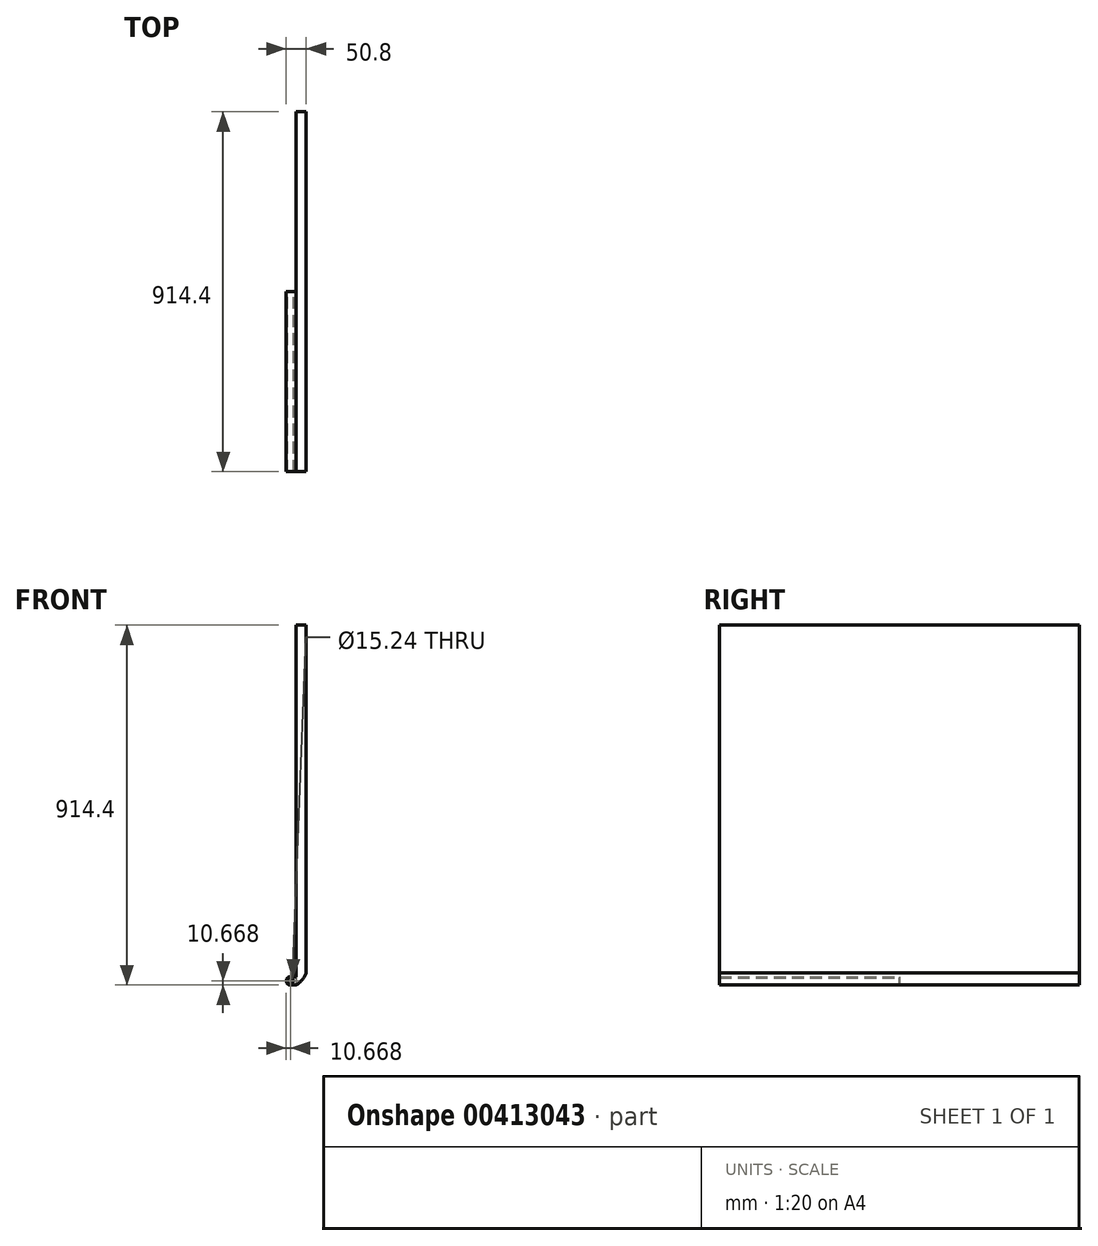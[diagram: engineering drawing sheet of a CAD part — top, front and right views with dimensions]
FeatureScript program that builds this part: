
annotation { "Feature Type Name" : "Feature", "Feature Type Description" : "" }
export const myFeature = defineFeature(function(context is Context, id is Id, definition is map)
    precondition{}
    {
        {
            var Q0;
            Q0=qCreatedBy(makeId("Right.planeOp"),FACE);
            var sketch = newSketch(context, id + "F0", { "sketchPlane" : qUnion([Q0])});
            skLineSegment(sketch, "E0.bottom", {"start": v(457.2, -457.2) * mm, "end": v(-457.2, -457.2) * mm});
            skLineSegment(sketch, "E0.top", {"start": v(457.2, 457.2) * mm, "end": v(-457.2, 457.2) * mm});
            skLineSegment(sketch, "E0.left", {"start": v(457.2, -457.2) * mm, "end": v(457.2, 457.2) * mm});
            skLineSegment(sketch, "E0.right", {"start": v(-457.2, -457.2) * mm, "end": v(-457.2, 457.2) * mm});
            skPoint(sketch, "E0.middle", {"position": v(0, 0) * mm});
            skSolve(sketch);
        }
        {
            var Q0;
            Q0=makeQuery(id+"F0.imprint","IMPRINT",FACE,{"disambiguationData":[TD([[makeQuery(id+"F0.imprint","IMPRINT",EDGE,{"derivedFrom":sQuery(id+"F0.wireOp",EDGE,"E0.bottom")}),-1.0]])]});
            extrude(context, id + "F1", {"entities" : qUnion([Q0]), "depth" : 25.4 * mm});
        }
        {
            var Q0;
            Q0=qCreatedBy(makeId("Front.planeOp"),FACE);
            var sketch = newSketch(context, id + "F2", { "sketchPlane" : qUnion([Q0])});
            skArc(sketch, "E1", {"start": v(-14.73, -435.86) * mm, "mid": v(-25.4, -446.53) * mm, "end": v(-14.73, -457.2) * mm});
            skLineSegment(sketch, "E2", {"start": v(-25.4, -446.53) * mm, "end": v(-25.4, -527.35) * mm, "construction": true});
            skLineSegment(sketch, "E3", {"start": v(0, -457.2) * mm, "end": v(-47.92, -457.2) * mm, "construction": true});
            skCircle(sketch, "E4.0", {"center": v(-14.73, -446.53) * mm, "radius": 7.62 * mm});
            skLineSegment(sketch, "E5", {"start": v(-14.73, -435.86) * mm, "end": v(0, -435.86) * mm});
            skLineSegment(sketch, "E6", {"start": v(0, -435.86) * mm, "end": v(0, -457.2) * mm});
            skLineSegment(sketch, "E7", {"start": v(0, -457.2) * mm, "end": v(-14.73, -457.2) * mm});
            skSolve(sketch);
        }
        {
            var Q0;
            Q0=makeQuery(id+"F2.imprint","IMPRINT",FACE,{"disambiguationData":[TD([[makeQuery(id+"F2.imprint","IMPRINT",EDGE,{"derivedFrom":sQuery(id+"F2.wireOp",EDGE,"E1")}),1.0]])]});
            var Q1;
            Q1=makeQuery(id+"F1.opExtrude","CAP_VERTEX",VERTEX,{"disambiguationData":[OSD([sQuery(id+"F0.wireOp",EDGE,"E0.bottom"),sQuery(id+"F0.wireOp",EDGE,"E0.right")])],"isStart":true});
            extrude(context, id + "F3", {"entities" : qUnion([Q0]), "operationType" : NewBodyOperationType.ADD, "endBound" : BoundingType.UP_TO_VERTEX, "endBoundEntityVertex" : qUnion([Q1]), "depth" : 30.48 * mm});
        }
        {
            var Q0;
            Q0=makeQuery(id+"F3.boolean.opBoolean","MERGE",FACE,{"derivedFrom":[makeQuery(id+"F1.opExtrude","SWEPT_FACE",FACE,{"disambiguationData":[OSD([sQuery(id+"F0.wireOp",EDGE,"E0.right")])]}),makeQuery(id+"F3.opExtrude","CAP_FACE",FACE,{"disambiguationData":[OSD([dummyQuery(id+"F3.vertexPlane.planeOp",FACE)])],"isStart":false})]});
            var sketch = newSketch(context, id + "F4", { "sketchPlane" : qUnion([Q0])});
            skArc(sketch, "E8", {"start": v(0, -457.2) * mm, "mid": v(15.23, -443.47) * mm, "end": v(25.4, -425.66) * mm});
            skPoint(sketch, "E8.startSnap0", {"position": v(5.33, -457.2) * mm});
            skLineSegment(sketch, "E9", {"start": v(25.4, -425.66) * mm, "end": v(25.4, -457.2) * mm});
            skLineSegment(sketch, "E10", {"start": v(25.4, -457.2) * mm, "end": v(0, -457.2) * mm});
            skSolve(sketch);
        }
        {
            var Q0;
            Q0=makeQuery(id+"F4.imprint","IMPRINT",FACE,{"disambiguationData":[TD([[makeQuery(id+"F4.imprint","IMPRINT",EDGE,{"derivedFrom":sQuery(id+"F4.wireOp",EDGE,"E8")}),-1.0]])]});
            var Q1;
            Q1=makeQuery(id+"F1.opExtrude","SWEPT_FACE",FACE,{"disambiguationData":[OSD([sQuery(id+"F0.wireOp",EDGE,"E0.left")])]});
            extrude(context, id + "F5", {"entities" : qUnion([Q0]), "operationType" : NewBodyOperationType.REMOVE, "endBound" : BoundingType.UP_TO_SURFACE, "oppositeDirection" : true, "endBoundEntityFace" : qUnion([Q1]), "depth" : 30.48 * mm});
        }
    });
